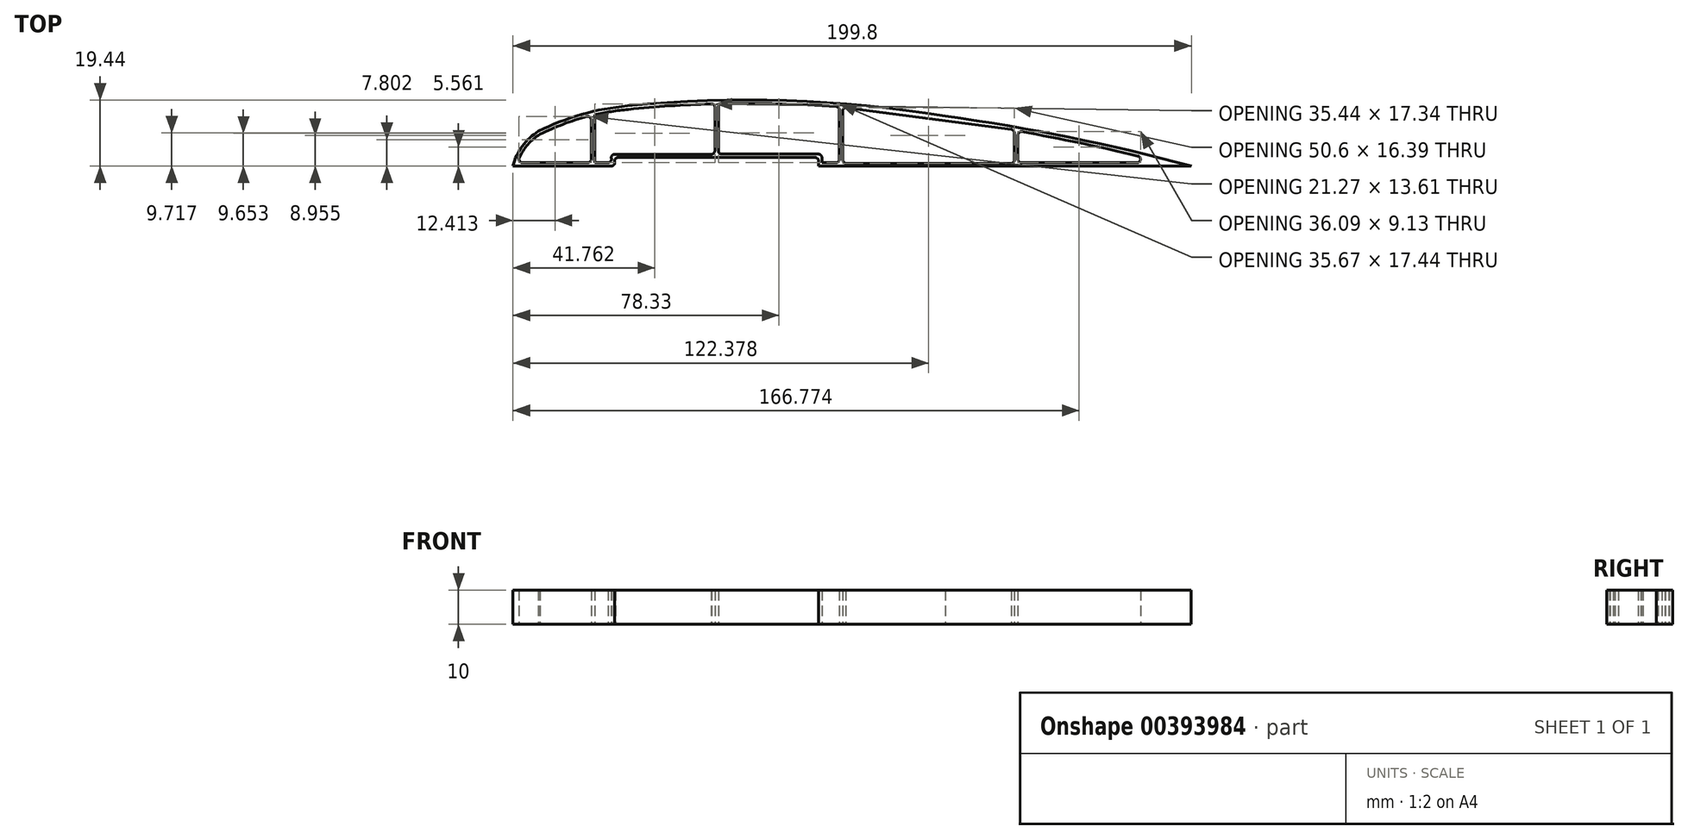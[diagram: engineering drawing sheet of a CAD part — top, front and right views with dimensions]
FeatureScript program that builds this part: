
annotation { "Feature Type Name" : "Feature", "Feature Type Description" : "" }
export const myFeature = defineFeature(function(context is Context, id is Id, definition is map)
    precondition{}
    {
        {
            var Q0;
            Q0=qCreatedBy(makeId("Top.planeOp"),FACE);
            var sketch = newSketch(context, id + "F0", { "sketchPlane" : qUnion([Q0])});
            skLineSegment(sketch, "E0", {"start": v(-450.4, -35.98) * mm, "end": v(-421.4, -35.98) * mm});
            skLineSegment(sketch, "E1", {"start": v(-360.4, -35.98) * mm, "end": v(-250.6, -35.98) * mm});
            skLineSegment(sketch, "E2", {"start": v(-447.62, -34.98) * mm, "end": v(-428.35, -34.98) * mm});
            skArc(sketch, "E3", {"start": v(-428.35, -34.98) * mm, "mid": v(-427.65, -34.69) * mm, "end": v(-427.35, -33.98) * mm});
            skLineSegment(sketch, "E4", {"start": v(-426.35, -34.98) * mm, "end": v(-422.4, -34.98) * mm});
            skLineSegment(sketch, "E5", {"start": v(-359.4, -34.98) * mm, "end": v(-355.24, -34.98) * mm});
            skLineSegment(sketch, "E6", {"start": v(-352.24, -34.98) * mm, "end": v(-303.67, -34.98) * mm});
            skArc(sketch, "E7", {"start": v(-353.24, -33.98) * mm, "mid": v(-352.94, -34.69) * mm, "end": v(-352.24, -34.98) * mm});
            skLineSegment(sketch, "E8", {"start": v(-300.67, -34.98) * mm, "end": v(-266.58, -34.98) * mm});
            skArc(sketch, "E9", {"start": v(-301.67, -33.98) * mm, "mid": v(-301.38, -34.69) * mm, "end": v(-300.67, -34.98) * mm});
            skArc(sketch, "E10", {"start": v(-442.88, -25.75) * mm, "mid": v(-447.67, -30.1) * mm, "end": v(-450.4, -35.98) * mm});
            skArc(sketch, "E11", {"start": v(-442.36, -26.6) * mm, "mid": v(-446, -29.61) * mm, "end": v(-448.54, -33.58) * mm});
            skArc(sketch, "E12", {"start": v(-448.54, -33.58) * mm, "mid": v(-448.46, -34.53) * mm, "end": v(-447.62, -34.98) * mm});
            skArc(sketch, "E13", {"start": v(-416.61, -18.27) * mm, "mid": v(-430.1, -20.78) * mm, "end": v(-442.88, -25.75) * mm});
            skArc(sketch, "E14", {"start": v(-416.52, -19.26) * mm, "mid": v(-421.46, -19.88) * mm, "end": v(-426.35, -20.84) * mm});
            skArc(sketch, "E15", {"start": v(-428.61, -21.4) * mm, "mid": v(-435.65, -23.67) * mm, "end": v(-442.43, -26.64) * mm});
            skArc(sketch, "E16", {"start": v(-427.35, -22.37) * mm, "mid": v(-427.74, -21.58) * mm, "end": v(-428.61, -21.4) * mm});
            skArc(sketch, "E17", {"start": v(-323.03, -21.29) * mm, "mid": v(-369.72, -16.73) * mm, "end": v(-416.61, -18.27) * mm});
            skArc(sketch, "E18", {"start": v(-323.19, -22.27) * mm, "mid": v(-337.64, -20.2) * mm, "end": v(-352.16, -18.73) * mm});
            skArc(sketch, "E19", {"start": v(-352.16, -18.73) * mm, "mid": v(-352.91, -19) * mm, "end": v(-353.24, -19.73) * mm});
            skArc(sketch, "E20", {"start": v(-355.16, -18.5) * mm, "mid": v(-372.03, -17.66) * mm, "end": v(-388.92, -17.62) * mm});
            skArc(sketch, "E21", {"start": v(-354.24, -19.5) * mm, "mid": v(-354.5, -18.81) * mm, "end": v(-355.16, -18.5) * mm});
            skArc(sketch, "E22", {"start": v(-388.92, -17.62) * mm, "mid": v(-389.62, -17.92) * mm, "end": v(-389.9, -18.62) * mm});
            skArc(sketch, "E23", {"start": v(-391.93, -17.7) * mm, "mid": v(-404.24, -18.27) * mm, "end": v(-416.51, -19.26) * mm});
            skArc(sketch, "E24", {"start": v(-390.9, -18.7) * mm, "mid": v(-391.2, -17.98) * mm, "end": v(-391.93, -17.7) * mm});
            skArc(sketch, "E25", {"start": v(-250.6, -35.98) * mm, "mid": v(-286.59, -27.5) * mm, "end": v(-323.03, -21.29) * mm});
            skArc(sketch, "E26", {"start": v(-266.34, -33) * mm, "mid": v(-283.37, -29.19) * mm, "end": v(-300.5, -25.87) * mm});
            skArc(sketch, "E27", {"start": v(-266.58, -34.98) * mm, "mid": v(-265.58, -34.1) * mm, "end": v(-266.34, -33) * mm});
            skArc(sketch, "E28", {"start": v(-300.5, -25.87) * mm, "mid": v(-301.31, -26.09) * mm, "end": v(-301.67, -26.85) * mm});
            skArc(sketch, "E29", {"start": v(-303.5, -25.34) * mm, "mid": v(-313.32, -23.73) * mm, "end": v(-323.17, -22.28) * mm});
            skArc(sketch, "E30", {"start": v(-302.67, -26.33) * mm, "mid": v(-302.9, -25.68) * mm, "end": v(-303.5, -25.34) * mm});
            skArc(sketch, "E31", {"start": v(-421.4, -35.98) * mm, "mid": v(-420.61, -35.6) * mm, "end": v(-420.44, -34.73) * mm});
            skArc(sketch, "E32", {"start": v(-419.47, -33.48) * mm, "mid": v(-420.26, -33.87) * mm, "end": v(-420.44, -34.73) * mm});
            skLineSegment(sketch, "E33", {"start": v(-421.4, -33.98) * mm, "end": v(-421.4, -33.48) * mm});
            skArc(sketch, "E34", {"start": v(-422.4, -34.98) * mm, "mid": v(-421.7, -34.69) * mm, "end": v(-421.4, -33.98) * mm});
            skArc(sketch, "E35", {"start": v(-420.4, -32.48) * mm, "mid": v(-421.11, -32.77) * mm, "end": v(-421.4, -33.48) * mm});
            skLineSegment(sketch, "E36", {"start": v(-360.4, -34.48) * mm, "end": v(-360.4, -35.98) * mm});
            skArc(sketch, "E37", {"start": v(-360.4, -34.48) * mm, "mid": v(-360.7, -33.77) * mm, "end": v(-361.4, -33.48) * mm});
            skLineSegment(sketch, "E38", {"start": v(-359.4, -33.48) * mm, "end": v(-359.4, -34.98) * mm});
            skArc(sketch, "E39", {"start": v(-359.4, -33.48) * mm, "mid": v(-359.7, -32.77) * mm, "end": v(-360.4, -32.48) * mm});
            skLineSegment(sketch, "E40", {"start": v(-427.35, -33.98) * mm, "end": v(-427.35, -22.37) * mm});
            skLineSegment(sketch, "E41", {"start": v(-426.35, -34.98) * mm, "end": v(-426.35, -20.84) * mm});
            skLineSegment(sketch, "E42", {"start": v(-353.24, -33.98) * mm, "end": v(-353.24, -19.73) * mm});
            skLineSegment(sketch, "E43", {"start": v(-354.24, -33.98) * mm, "end": v(-354.24, -19.5) * mm});
            skArc(sketch, "E44", {"start": v(-355.24, -34.98) * mm, "mid": v(-354.53, -34.69) * mm, "end": v(-354.24, -33.98) * mm});
            skLineSegment(sketch, "E45", {"start": v(-301.67, -33.98) * mm, "end": v(-301.67, -26.85) * mm});
            skLineSegment(sketch, "E46", {"start": v(-302.67, -33.98) * mm, "end": v(-302.67, -26.33) * mm});
            skArc(sketch, "E47", {"start": v(-303.67, -34.98) * mm, "mid": v(-302.96, -34.69) * mm, "end": v(-302.67, -33.98) * mm});
            skLineSegment(sketch, "E48", {"start": v(-389.9, -31.48) * mm, "end": v(-389.9, -18.62) * mm});
            skLineSegment(sketch, "E49", {"start": v(-390.9, -31.48) * mm, "end": v(-390.9, -18.7) * mm});
            skLineSegment(sketch, "E50", {"start": v(-420.4, -32.48) * mm, "end": v(-391.9, -32.48) * mm});
            skArc(sketch, "E51", {"start": v(-391.9, -32.48) * mm, "mid": v(-391.2, -32.19) * mm, "end": v(-390.9, -31.48) * mm});
            skLineSegment(sketch, "E52", {"start": v(-388.9, -32.48) * mm, "end": v(-360.4, -32.48) * mm});
            skArc(sketch, "E53", {"start": v(-389.9, -31.48) * mm, "mid": v(-389.61, -32.19) * mm, "end": v(-388.9, -32.48) * mm});
            skLineSegment(sketch, "E54", {"start": v(-419.47, -33.48) * mm, "end": v(-361.4, -33.48) * mm});
            skSolve(sketch);
        }
        {
            var Q0;
            Q0=makeQuery(id+"F0.imprint","IMPRINT",FACE,{"disambiguationData":[TD([[makeQuery(id+"F0.imprint","IMPRINT",EDGE,{"derivedFrom":sQuery(id+"F0.wireOp",EDGE,"E2")}),1.0]])]});
            var sketch = newSketch(context, id + "F1", { "sketchPlane" : qUnion([Q0])});
            skLineSegment(sketch, "E55", {"start": v(-426.36, -34.97) * mm, "end": v(-426.36, -20.88) * mm});
            skArc(sketch, "E56", {"start": v(-416.45, -19.3) * mm, "mid": v(-421.43, -19.93) * mm, "end": v(-426.36, -20.88) * mm});
            skArc(sketch, "E57", {"start": v(-391.96, -17.66) * mm, "mid": v(-404.22, -18.27) * mm, "end": v(-416.45, -19.3) * mm});
            skArc(sketch, "E58", {"start": v(-390.92, -18.73) * mm, "mid": v(-391.19, -17.94) * mm, "end": v(-391.96, -17.66) * mm});
            skLineSegment(sketch, "E59", {"start": v(-390.92, -18.73) * mm, "end": v(-390.92, -31.4) * mm});
            skArc(sketch, "E60", {"start": v(-391.88, -32.53) * mm, "mid": v(-391.2, -32.15) * mm, "end": v(-390.92, -31.4) * mm});
            skLineSegment(sketch, "E61", {"start": v(-391.88, -32.53) * mm, "end": v(-420.4, -32.53) * mm});
            skArc(sketch, "E62", {"start": v(-420.26, -32.53) * mm, "mid": v(-421.06, -32.73) * mm, "end": v(-421.44, -33.47) * mm});
            skArc(sketch, "E63", {"start": v(-422.39, -35) * mm, "mid": v(-421.7, -34.68) * mm, "end": v(-421.4, -33.97) * mm});
            skLineSegment(sketch, "E64", {"start": v(-421.4, -33.97) * mm, "end": v(-421.44, -33.47) * mm});
            skLineSegment(sketch, "E65", {"start": v(-426.36, -34.97) * mm, "end": v(-422.39, -35) * mm});
            skLineSegment(sketch, "E66", {"start": v(-353.32, -33.97) * mm, "end": v(-353.32, -19.68) * mm});
            skLineSegment(sketch, "E67", {"start": v(-352.34, -35.22) * mm, "end": v(-303.74, -35.22) * mm});
            skLineSegment(sketch, "E68", {"start": v(-302.75, -33.96) * mm, "end": v(-302.75, -26.22) * mm});
            skLineSegment(sketch, "E69", {"start": v(-352.13, -18.83) * mm, "end": v(-303.6, -25.23) * mm});
            skArc(sketch, "E70", {"start": v(-353.32, -33.97) * mm, "mid": v(-353.05, -34.77) * mm, "end": v(-352.34, -35.22) * mm});
            skArc(sketch, "E71", {"start": v(-303.74, -35.22) * mm, "mid": v(-302.94, -34.83) * mm, "end": v(-302.75, -33.96) * mm});
            skArc(sketch, "E72", {"start": v(-302.75, -26.22) * mm, "mid": v(-303, -25.57) * mm, "end": v(-303.6, -25.23) * mm});
            skArc(sketch, "E73", {"start": v(-352.13, -18.83) * mm, "mid": v(-352.89, -19.02) * mm, "end": v(-353.32, -19.68) * mm});
            skSolve(sketch);
        }
        {
            var Q0;
            Q0 = qSketchRegion(id + "F0", true);
            extrude(context, id + "F2", {"entities" : qUnion([Q0]), "depth" : 10 * mm});
        }
        {
            var Q0;
            Q0 = qSketchRegion(id + "F1", true);
            extrude(context, id + "F3", {"entities" : qUnion([Q0]), "operationType" : NewBodyOperationType.REMOVE, "depth" : 25 * mm});
        }
    });
